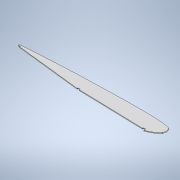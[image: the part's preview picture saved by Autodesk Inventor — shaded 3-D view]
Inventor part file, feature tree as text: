
AUTODESK INVENTOR PART (.ipt)
format: ipt  version: 2022 (Build 260153000, 153)  size: 363,520 bytes
history: native  units: mm
features: extrude x1, sketch x1
ambient origin geometry x8: Origin, YZ Plane, XZ Plane, XY Plane, X Axis, Y Axis, Z Axis, Center Point
bodies: Body1 (feature_tree)
feature tree (2):
  extrude  "Extrusion5"  Depth=368.759386mm
  sketch  "Sketch1"  dims[d31=34.456mm d50=368.759386mm d57=16.0mm d69=8.0mm d80=19.0mm d81=16.0mm d82=1.0mm d83=1.0mm d84=1.0mm d85=1.0mm d86=1.0mm d87=0.8mm d88=1.0mm d90=19.0mm d94=5.0mm d95=5.0mm d105=5.0mm d106=5.0mm d108=2.0mm d114=5.0mm d115=5.0mm d116=24.0mm d117=2.5mm d118=2.5mm d123=2.5mm d124=2.5mm d125=10.0mm d126=24.0mm d127=24.0mm d128=27.0mm d135=0.5mm d139=7.0mm d169=27.0mm d181=45.0deg d185=7.0mm d186=45.0deg d190=7.0mm d191=45.0deg d206=90.0deg d212=90.0deg d215=7.0mm d216=90.0deg d219=7.0mm d220=2.0mm d221=0.0mm]
